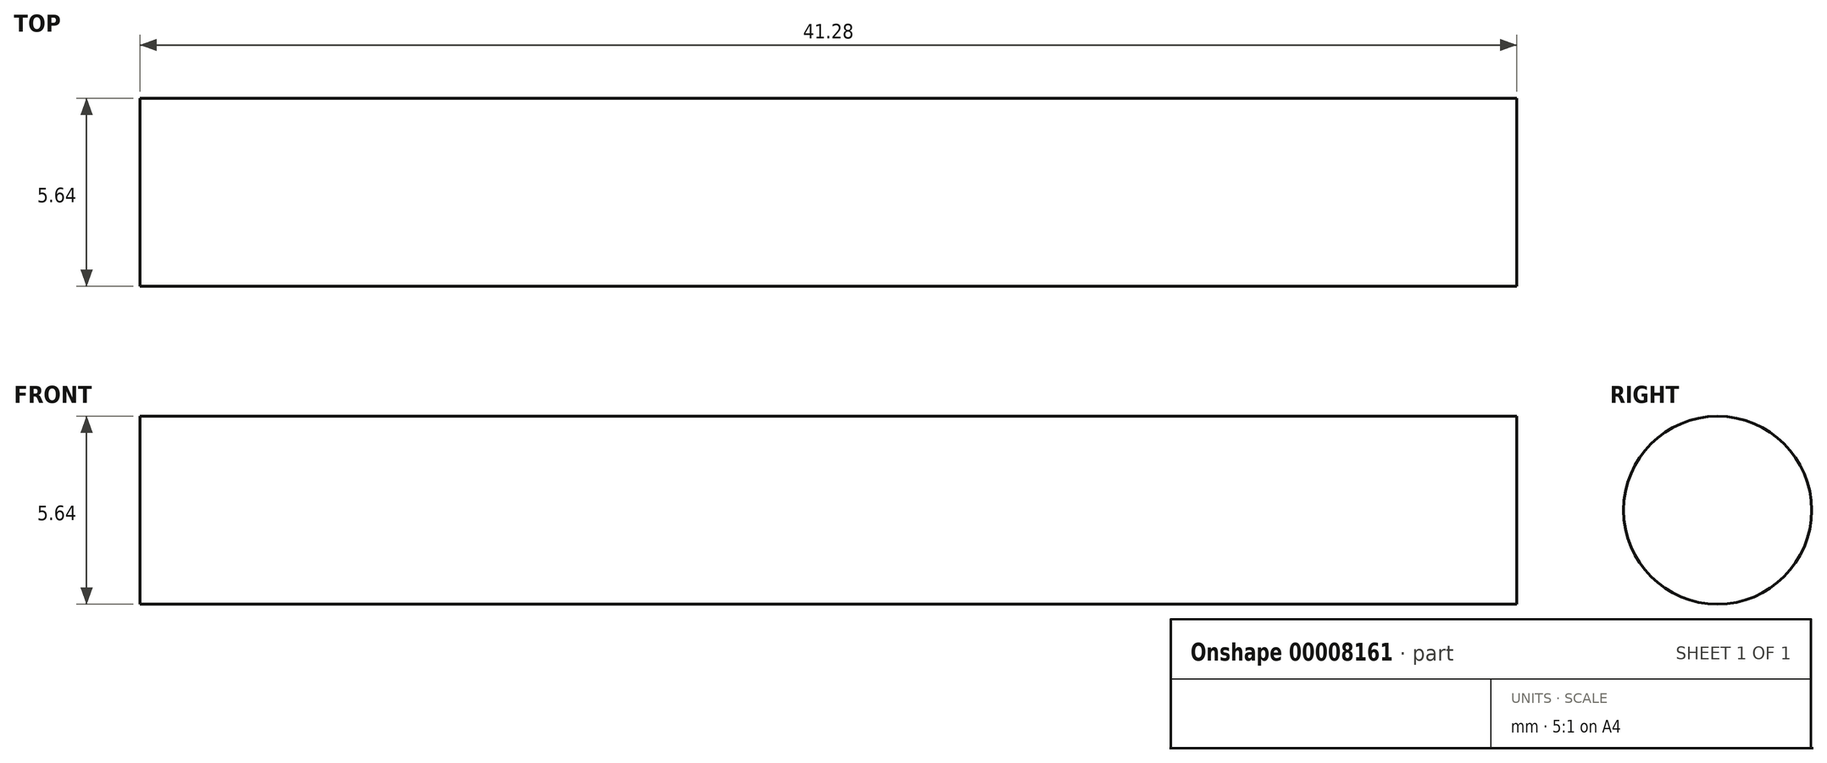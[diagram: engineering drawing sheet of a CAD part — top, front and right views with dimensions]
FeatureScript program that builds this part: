
annotation { "Feature Type Name" : "Feature", "Feature Type Description" : "" }
export const myFeature = defineFeature(function(context is Context, id is Id, definition is map)
    precondition{}
    {
        {
            var Q0;
            Q0=qCreatedBy(makeId("Right.planeOp"),FACE);
            var sketch = newSketch(context, id + "F0", { "sketchPlane" : qUnion([Q0])});
            skCircle(sketch, "E0", {"center": v(0, 0) * mm, "radius": 2.82 * mm});
            skSolve(sketch);
        }
        {
            var Q0;
            Q0 = qSketchRegion(id + "F0", true);
            extrude(context, id + "F1", {"entities" : qUnion([Q0]), "oppositeDirection" : true, "depth" : 41.27 * mm});
        }
    });
